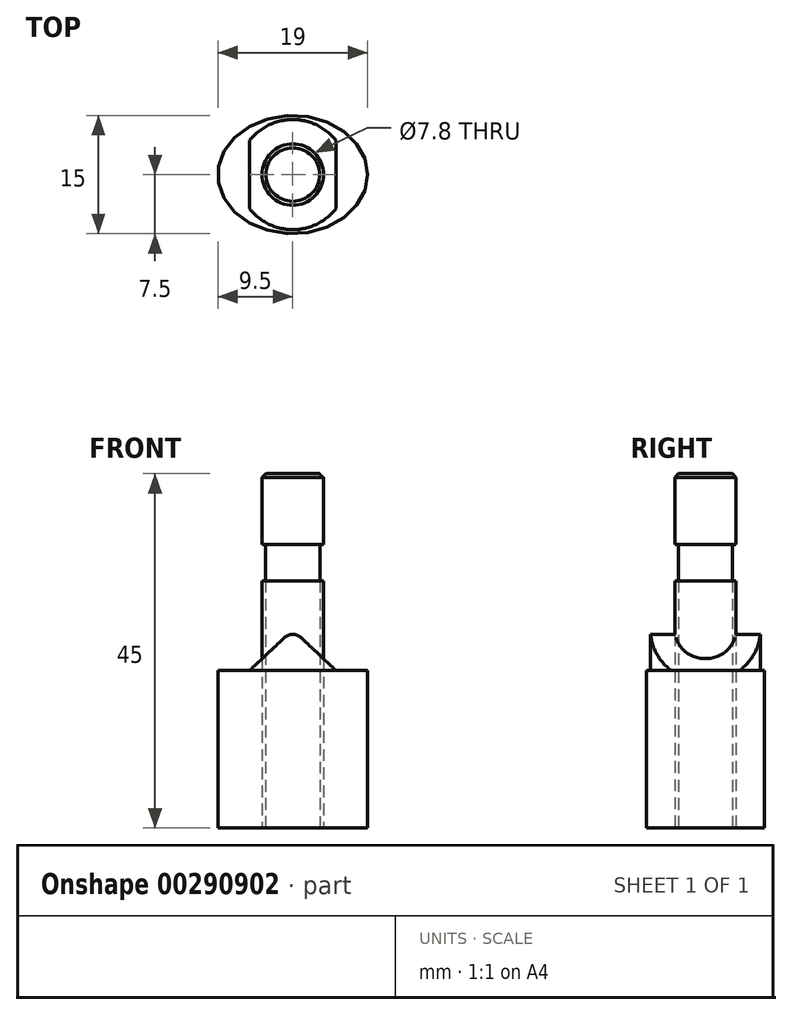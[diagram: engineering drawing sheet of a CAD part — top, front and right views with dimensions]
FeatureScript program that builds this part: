
annotation { "Feature Type Name" : "Feature", "Feature Type Description" : "" }
export const myFeature = defineFeature(function(context is Context, id is Id, definition is map)
    precondition{}
    {
        {
            var Q0;
            Q0=qCreatedBy(makeId("Top.planeOp"),FACE);
            var sketch = newSketch(context, id + "F0", { "sketchPlane" : qUnion([Q0])});
            skEllipse(sketch, "E0", {"center": v(0, 0) * mm, "majorRadius": 9.5 * mm, "minorRadius": 7.5 * mm, "majorAxis": v(1, 0)});
            skSolve(sketch);
        }
        {
            var Q0;
            Q0=makeQuery(id+"F0.imprint","IMPRINT",FACE,{"disambiguationData":[TD([[makeQuery(id+"F0.imprint","IMPRINT",EDGE,{"derivedFrom":sQuery(id+"F0.wireOp",EDGE,"E0")}),1.0]])]});
            extrude(context, id + "F1", {"entities" : qUnion([Q0]), "depth" : 20 * mm});
        }
        {
            var Q0;
            Q0=makeQuery(id+"F1.opExtrude","CAP_FACE",FACE,{"disambiguationData":[OSD([sQuery(id+"F0.wireOp",EDGE,"E0")])],"isStart":false});
            var sketch = newSketch(context, id + "F2", { "sketchPlane" : qUnion([Q0])});
            skCircle(sketch, "E1", {"center": v(0, 0) * mm, "radius": 7 * mm});
            skSolve(sketch);
        }
        {
            var Q0;
            Q0=makeQuery(id+"F2.imprint","IMPRINT",FACE,{"disambiguationData":[TD([[makeQuery(id+"F2.imprint","IMPRINT",EDGE,{"derivedFrom":sQuery(id+"F2.wireOp",EDGE,"E1")}),1.0]])]});
            extrude(context, id + "F3", {"entities" : qUnion([Q0]), "operationType" : NewBodyOperationType.ADD, "depth" : 4.6 * mm});
        }
        {
            var Q0;
            Q0=qCreatedBy(makeId("Front.planeOp"),FACE);
            var sketch = newSketch(context, id + "F4", { "sketchPlane" : qUnion([Q0])});
            skLineSegment(sketch, "E2.top", {"start": v(0, 24.6) * mm, "end": v(0, 24.6) * mm});
            skLineSegment(sketch, "E3", {"start": v(-5.5, 20) * mm, "end": v(-1.03, 24.2) * mm});
            skLineSegment(sketch, "E4", {"start": v(1.03, 24.2) * mm, "end": v(5.5, 20) * mm});
            skPoint(sketch, "E5.visualSharp", {"position": v(-0.6, 24.6) * mm});
            skArc(sketch, "E5.filletArc", {"start": v(0, 24.6) * mm, "mid": v(-0.55, 24.5) * mm, "end": v(-1.03, 24.2) * mm});
            skPoint(sketch, "E6.visualSharp", {"position": v(0.6, 24.6) * mm});
            skArc(sketch, "E6.filletArc", {"start": v(1.03, 24.2) * mm, "mid": v(0.55, 24.5) * mm, "end": v(0, 24.6) * mm});
            skLineSegment(sketch, "E7", {"start": v(-5.5, 20) * mm, "end": v(-7.13, 20) * mm});
            skLineSegment(sketch, "E8", {"start": v(-7.13, 20) * mm, "end": v(-7.13, 24.6) * mm});
            skLineSegment(sketch, "E9", {"start": v(-7.13, 24.6) * mm, "end": v(7.3, 24.6) * mm});
            skLineSegment(sketch, "E10", {"start": v(7.3, 24.6) * mm, "end": v(7.3, 20) * mm});
            skLineSegment(sketch, "E11", {"start": v(7.3, 20) * mm, "end": v(5.5, 20) * mm});
            skSolve(sketch);
        }
        {
            var Q0;
            Q0=qSketchRegion(id+"F4",true);
            extrude(context, id + "F5", {"entities" : qUnion([Q0]), "operationType" : NewBodyOperationType.REMOVE, "endBound" : BoundingType.SYMMETRIC, "oppositeDirection" : true, "depth" : 25 * mm});
        }
        {
            var Q0;
            Q0=makeQuery(id+"F1.opExtrude","CAP_FACE",FACE,{"disambiguationData":[OSD([sQuery(id+"F0.wireOp",EDGE,"E0")])],"isStart":true});
            var sketch = newSketch(context, id + "F6", { "sketchPlane" : qUnion([Q0])});
            skCircle(sketch, "E12", {"center": v(0, 0) * mm, "radius": 3.9 * mm});
            skSolve(sketch);
        }
        {
            var Q0;
            Q0=makeQuery(id+"F6.imprint","IMPRINT",FACE,{"disambiguationData":[TD([[makeQuery(id+"F6.imprint","IMPRINT",EDGE,{"derivedFrom":sQuery(id+"F6.wireOp",EDGE,"E12")}),1.0]])]});
            extrude(context, id + "F7", {"entities" : qUnion([Q0]), "operationType" : NewBodyOperationType.REMOVE, "endBound" : BoundingType.THROUGH_ALL, "oppositeDirection" : true, "depth" : 25 * mm});
        }
        {
            var Q0;
            Q0=qCreatedBy(makeId("Top.planeOp"),FACE);
            var sketch = newSketch(context, id + "F8", { "sketchPlane" : qUnion([Q0])});
            skCircle(sketch, "E13", {"center": v(0, 0) * mm, "radius": 3.45 * mm});
            skSolve(sketch);
        }
        {
            var Q0;
            Q0=qSketchRegion(id+"F8",true);
            extrude(context, id + "F9", {"entities" : qUnion([Q0]), "operationType" : NewBodyOperationType.ADD, "depth" : 45 * mm});
        }
        {
            var Q0;
            Q0=qCreatedBy(makeId("Top.planeOp"),FACE);
            var sketch = newSketch(context, id + "F10", { "sketchPlane" : qUnion([Q0])});
            skCircle(sketch, "E14", {"center": v(0, 0) * mm, "radius": 3.9 * mm});
            skSolve(sketch);
        }
        {
            var Q0;
            Q0=qSketchRegion(id+"F10",true);
            extrude(context, id + "F11", {"entities" : qUnion([Q0]), "depth" : 31.4 * mm});
        }
        {
            var Q0;
            Q0=makeQuery(id+"F9.opExtrude","CAP_FACE",FACE,{"disambiguationData":[OSD([sQuery(id+"F8.wireOp",EDGE,"E13")])],"isStart":false});
            var sketch = newSketch(context, id + "F12", { "sketchPlane" : qUnion([Q0])});
            skCircle(sketch, "E15", {"center": v(0, 0) * mm, "radius": 3.9 * mm});
            skSolve(sketch);
        }
        {
            var Q0;
            Q0=qSketchRegion(id+"F12",true);
            extrude(context, id + "F13", {"entities" : qUnion([Q0]), "operationType" : NewBodyOperationType.ADD, "oppositeDirection" : true, "depth" : 9 * mm});
        }
        {
            var Q0;
            Q0=makeQuery(id+"F13.opExtrude","CAP_EDGE",EDGE,{"disambiguationData":[OSD([sQuery(id+"F12.wireOp",EDGE,"E15")])],"isStart":true});
            chamfer(context, id + "F14", {"entities" : qUnion([Q0]), "width" : 0.5 * mm, "tangentPropagation" : true});
        }
    });
